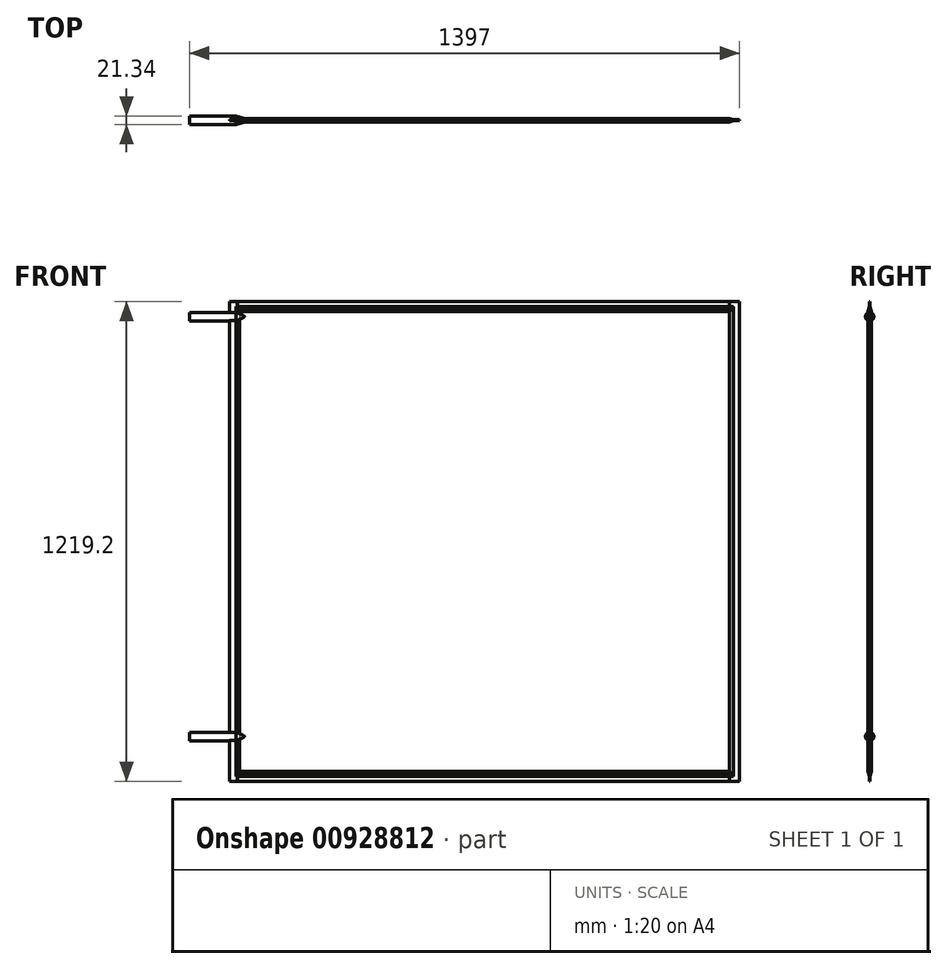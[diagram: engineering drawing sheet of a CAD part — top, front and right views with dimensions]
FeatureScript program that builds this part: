
annotation { "Feature Type Name" : "Feature", "Feature Type Description" : "" }
export const myFeature = defineFeature(function(context is Context, id is Id, definition is map)
    precondition{}
    {
        {
            var Q0;
            Q0=qCreatedBy(makeId("Front.planeOp"),FACE);
            var sketch = newSketch(context, id + "F0", { "sketchPlane" : qUnion([Q0])});
            skLineSegment(sketch, "E0", {"start": v(-991.5, -804.5) * mm, "end": v(-775.6, -1267.5) * mm});
            skLineSegment(sketch, "E1", {"start": v(-991.5, -804.5) * mm, "end": v(-991.5, -829.18) * mm});
            skLineSegment(sketch, "E2", {"start": v(-775.6, -1267.5) * mm, "end": v(-380.3, -1083.18) * mm});
            skLineSegment(sketch, "E3", {"start": v(-380.3, -1083.18) * mm, "end": v(-380.3, -829.18) * mm, "construction": true});
            skLineSegment(sketch, "E4", {"start": v(-991.5, -829.18) * mm, "end": v(-380.3, -829.18) * mm, "construction": true});
            skLineSegment(sketch, "E5", {"start": v(76.1, -804.5) * mm, "end": v(76.1, -359.45) * mm, "construction": true});
            skLineSegment(sketch, "E6", {"start": v(-685.9, -829.18) * mm, "end": v(-685.9, -1225.68) * mm, "construction": true});
            skLineSegment(sketch, "E7.MirrorCS", {"start": v(838.1, -829.18) * mm, "end": v(838.1, -1225.68) * mm, "construction": true});
            skLineSegment(sketch, "E8.MirrorCS", {"start": v(1143.7, -804.5) * mm, "end": v(927.8, -1267.5) * mm, "construction": true});
            skLineSegment(sketch, "E9.MirrorCS", {"start": v(1143.7, -804.5) * mm, "end": v(1143.7, -829.18) * mm, "construction": true});
            skLineSegment(sketch, "E10.MirrorCS", {"start": v(927.8, -1267.5) * mm, "end": v(532.5, -1083.18) * mm, "construction": true});
            skLineSegment(sketch, "E11.MirrorCS", {"start": v(532.5, -1083.18) * mm, "end": v(532.5, -829.18) * mm, "construction": true});
            skLineSegment(sketch, "E12.MirrorCS", {"start": v(1143.7, -829.18) * mm, "end": v(532.5, -829.18) * mm, "construction": true});
            skLineSegment(sketch, "E13", {"start": v(-380.3, -1083.18) * mm, "end": v(76.1, -870.35) * mm});
            skLineSegment(sketch, "E14", {"start": v(76.1, -870.35) * mm, "end": v(532.5, -1083.18) * mm, "construction": true});
            skLineSegment(sketch, "E15", {"start": v(-991.5, -829.18) * mm, "end": v(-991.5, -359.45) * mm});
            skLineSegment(sketch, "E16", {"start": v(-991.5, -359.45) * mm, "end": v(-991.5, -3451.9) * mm, "construction": true});
            skLineSegment(sketch, "E17", {"start": v(-991.5, 1120.1) * mm, "end": v(1143.7, 1120.1) * mm, "construction": true});
            skLineSegment(sketch, "E18", {"start": v(-90.65, 1120.1) * mm, "end": v(-90.65, 1251.48) * mm, "construction": true});
            skLineSegment(sketch, "E19", {"start": v(-90.65, 1251.48) * mm, "end": v(242.85, 1251.48) * mm, "construction": true});
            skLineSegment(sketch, "E20", {"start": v(242.85, 1251.48) * mm, "end": v(242.85, 1120.1) * mm, "construction": true});
            skLineSegment(sketch, "E21", {"start": v(242.85, 1120.1) * mm, "end": v(-90.65, 1120.1) * mm});
            skPoint(sketch, "E22", {"position": v(76.1, 1120.1) * mm});
            skLineSegment(sketch, "E23", {"start": v(-101.7, 1120.1) * mm, "end": v(-101.7, 1251.48) * mm, "construction": true});
            skLineSegment(sketch, "E24", {"start": v(-101.7, 1251.48) * mm, "end": v(253.9, 1251.48) * mm, "construction": true});
            skLineSegment(sketch, "E25", {"start": v(253.9, 1251.48) * mm, "end": v(253.9, 1120.1) * mm, "construction": true});
            skLineSegment(sketch, "E26", {"start": v(253.9, 1120.1) * mm, "end": v(-101.7, 1120.1) * mm, "construction": true});
            skLineSegment(sketch, "E27", {"start": v(-991.5, -359.45) * mm, "end": v(-991.5, 700.03) * mm});
            skLineSegment(sketch, "E28", {"start": v(1143.7, 700.03) * mm, "end": v(1143.7, -829.18) * mm, "construction": true});
            skLineSegment(sketch, "E29", {"start": v(-991.5, 700.03) * mm, "end": v(-991.5, 1120.1) * mm});
            skLineSegment(sketch, "E30", {"start": v(1143.7, 700.03) * mm, "end": v(1143.7, 1120.1) * mm, "construction": true});
            skLineSegment(sketch, "E31", {"start": v(-90.65, 1120.1) * mm, "end": v(-991.5, 700.03) * mm, "construction": true});
            skLineSegment(sketch, "E32", {"start": v(253.9, 1120.1) * mm, "end": v(1143.7, 700.03) * mm, "construction": true});
            skLineSegment(sketch, "E33", {"start": v(-991.5, 1120.1) * mm, "end": v(76.1, 1120.1) * mm});
            skLineSegment(sketch, "E34", {"start": v(76.1, -870.35) * mm, "end": v(76.1, 1120.1) * mm});
            skSolve(sketch);
        }
        {
            var Q0;
            Q0=qCreatedBy(makeId("Front.planeOp"),FACE);
            var sketch = newSketch(context, id + "F1", { "sketchPlane" : qUnion([Q0])});
            skLineSegment(sketch, "E35.0", {"start": v(1422.3, 609.6) * mm, "end": v(1422.3, -609.6) * mm});
            skLineSegment(sketch, "E36", {"start": v(1422.3, -609.6) * mm, "end": v(126.9, -609.6) * mm});
            skLineSegment(sketch, "E37", {"start": v(1422.3, 609.6) * mm, "end": v(126.9, 609.6) * mm});
            skLineSegment(sketch, "E38", {"start": v(126.9, 609.6) * mm, "end": v(126.9, -609.6) * mm});
            skSolve(sketch);
        }
        {
            var Q0;
            Q0=qSketchRegion(id+"F1",true);
            extrude(context, id + "F2", {"entities" : qUnion([Q0]), "endBound" : BoundingType.SYMMETRIC, "depth" : 9.52 * mm, "offsetDistance" : 25.4 * mm});
        }
        {
            var Q0;
            Q0=qCreatedBy(makeId("Top.planeOp"),FACE);
            cPlane(context, id + "F3", {"entities" : qUnion([Q0]), "cplaneType" : CPlaneType.OFFSET, "offset" : 38.1 * mm, "width" : 152.4 * mm, "height" : 152.4 * mm});
        }
        {
            var Q0;
            Q0=qCreatedBy(makeId("Right.planeOp"),FACE);
            var sketch = newSketch(context, id + "F4", { "sketchPlane" : qUnion([Q0])});
            skLineSegment(sketch, "E39", {"start": v(1.21, 609.6) * mm, "end": v(1.21, 593.72) * mm});
            skLineSegment(sketch, "E40", {"start": v(1.21, 584.2) * mm, "end": v(4.76, 584.2) * mm, "construction": true});
            skLineSegment(sketch, "E41", {"start": v(8.31, 584.2) * mm, "end": v(8.31, 615.95) * mm});
            skLineSegment(sketch, "E42", {"start": v(-4.76, 0) * mm, "end": v(4.76, 0) * mm, "construction": true});
            skLineSegment(sketch, "E43", {"start": v(1.21, 596.9) * mm, "end": v(4.76, 584.2) * mm});
            skLineSegment(sketch, "E44", {"start": v(1.21, 593.72) * mm, "end": v(1.21, 584.2) * mm, "construction": true});
            skLineSegment(sketch, "E45", {"start": v(4.76, 584.2) * mm, "end": v(8.31, 584.2) * mm});
            skLineSegment(sketch, "E46", {"start": v(1.21, 609.6) * mm, "end": v(0, 609.6) * mm});
            skLineSegment(sketch, "E47", {"start": v(0, 609.6) * mm, "end": v(0, 615.95) * mm, "construction": true});
            skLineSegment(sketch, "E48", {"start": v(0, 615.95) * mm, "end": v(8.31, 615.95) * mm});
            skLineSegment(sketch, "E49.MirrorCS", {"start": v(-1.21, 609.6) * mm, "end": v(-1.21, 593.72) * mm});
            skLineSegment(sketch, "E50.MirrorCS", {"start": v(-1.21, 596.9) * mm, "end": v(-4.76, 584.2) * mm});
            skLineSegment(sketch, "E51.MirrorCS", {"start": v(-1.21, 609.6) * mm, "end": v(0, 609.6) * mm});
            skLineSegment(sketch, "E52.MirrorCS", {"start": v(0, 615.95) * mm, "end": v(-8.31, 615.95) * mm});
            skLineSegment(sketch, "E53.MirrorCS", {"start": v(-4.76, 584.2) * mm, "end": v(-8.31, 584.2) * mm});
            skLineSegment(sketch, "E54.MirrorCS", {"start": v(-8.31, 584.2) * mm, "end": v(-8.31, 615.95) * mm});
            skLineSegment(sketch, "E55.MirrorCS", {"start": v(-1.21, 593.72) * mm, "end": v(-1.21, 584.2) * mm, "construction": true});
            skLineSegment(sketch, "E56.MirrorCS", {"start": v(-1.21, 584.2) * mm, "end": v(-4.76, 584.2) * mm, "construction": true});
            skLineSegment(sketch, "E57.MirrorCS", {"start": v(1.21, -609.6) * mm, "end": v(0, -609.6) * mm});
            skLineSegment(sketch, "E58.MirrorCS", {"start": v(-1.21, -609.6) * mm, "end": v(0, -609.6) * mm});
            skLineSegment(sketch, "E59.MirrorCS", {"start": v(-8.31, -584.2) * mm, "end": v(-8.31, -615.95) * mm});
            skLineSegment(sketch, "E60.MirrorCS", {"start": v(0, -615.95) * mm, "end": v(8.31, -615.95) * mm});
            skLineSegment(sketch, "E61.MirrorCS", {"start": v(4.76, -584.2) * mm, "end": v(8.31, -584.2) * mm});
            skLineSegment(sketch, "E62.MirrorCS", {"start": v(1.21, -596.9) * mm, "end": v(4.76, -584.2) * mm});
            skLineSegment(sketch, "E63.MirrorCS", {"start": v(1.21, -609.6) * mm, "end": v(1.21, -593.72) * mm});
            skLineSegment(sketch, "E64.MirrorCS", {"start": v(1.21, -584.2) * mm, "end": v(4.76, -584.2) * mm, "construction": true});
            skLineSegment(sketch, "E65.MirrorCS", {"start": v(-1.21, -596.9) * mm, "end": v(-4.76, -584.2) * mm});
            skLineSegment(sketch, "E66.MirrorCS", {"start": v(8.31, -584.2) * mm, "end": v(8.31, -615.95) * mm});
            skLineSegment(sketch, "E67.MirrorCS", {"start": v(-4.76, -584.2) * mm, "end": v(-8.31, -584.2) * mm});
            skLineSegment(sketch, "E68.MirrorCS", {"start": v(1.21, -593.72) * mm, "end": v(1.21, -584.2) * mm, "construction": true});
            skLineSegment(sketch, "E69.MirrorCS", {"start": v(-1.21, -593.72) * mm, "end": v(-1.21, -584.2) * mm, "construction": true});
            skLineSegment(sketch, "E70.MirrorCS", {"start": v(-1.21, -609.6) * mm, "end": v(-1.21, -593.72) * mm});
            skLineSegment(sketch, "E71.MirrorCS", {"start": v(0, -615.95) * mm, "end": v(-8.31, -615.95) * mm});
            skLineSegment(sketch, "E72.MirrorCS", {"start": v(-1.21, -584.2) * mm, "end": v(-4.76, -584.2) * mm, "construction": true});
            skLineSegment(sketch, "E73.MirrorCS", {"start": v(0, -609.6) * mm, "end": v(0, -615.95) * mm, "construction": true});
            skSolve(sketch);
        }
        {
            var Q0;
            Q0=qSketchRegion(id+"F4",true);
            extrude(context, id + "F5", {"entities" : qUnion([Q0]), "operationType" : NewBodyOperationType.REMOVE, "endBound" : BoundingType.THROUGH_ALL, "depth" : 25.4 * mm, "offsetDistance" : 25.4 * mm});
        }
        {
            var Q0;
            Q0=qCreatedBy(makeId("Top.planeOp"),FACE);
            var sketch = newSketch(context, id + "F6", { "sketchPlane" : qUnion([Q0])});
            skLineSegment(sketch, "E74", {"start": v(126.9, 1.21) * mm, "end": v(142.77, 1.21) * mm});
            skLineSegment(sketch, "E75", {"start": v(152.3, 1.21) * mm, "end": v(152.3, 4.76) * mm, "construction": true});
            skLineSegment(sketch, "E76", {"start": v(152.3, 8.31) * mm, "end": v(120.55, 8.31) * mm});
            skLineSegment(sketch, "E77", {"start": v(774.6, 4.76) * mm, "end": v(774.6, -4.76) * mm, "construction": true});
            skLineSegment(sketch, "E78", {"start": v(142.77, 1.21) * mm, "end": v(152.3, 4.76) * mm});
            skLineSegment(sketch, "E79", {"start": v(142.77, 1.21) * mm, "end": v(152.3, 1.21) * mm, "construction": true});
            skLineSegment(sketch, "E80", {"start": v(152.3, 4.76) * mm, "end": v(152.3, 8.31) * mm});
            skLineSegment(sketch, "E81", {"start": v(126.9, 1.21) * mm, "end": v(126.9, 0) * mm});
            skLineSegment(sketch, "E82", {"start": v(126.9, 0) * mm, "end": v(120.55, 0) * mm, "construction": true});
            skLineSegment(sketch, "E83", {"start": v(120.55, 0) * mm, "end": v(120.55, 8.31) * mm});
            skLineSegment(sketch, "E84.MirrorCS", {"start": v(126.9, -1.21) * mm, "end": v(142.77, -1.21) * mm});
            skLineSegment(sketch, "E85.MirrorCS", {"start": v(152.3, -4.76) * mm, "end": v(142.77, -1.21) * mm});
            skLineSegment(sketch, "E86.MirrorCS", {"start": v(126.9, -1.21) * mm, "end": v(126.9, 0) * mm});
            skLineSegment(sketch, "E87.MirrorCS", {"start": v(120.55, 0) * mm, "end": v(120.55, -8.31) * mm});
            skLineSegment(sketch, "E88.MirrorCS", {"start": v(152.3, -4.76) * mm, "end": v(152.3, -8.31) * mm});
            skLineSegment(sketch, "E89.MirrorCS", {"start": v(152.3, -8.31) * mm, "end": v(120.55, -8.31) * mm});
            skLineSegment(sketch, "E90.MirrorCS", {"start": v(142.77, -1.21) * mm, "end": v(152.3, -1.21) * mm, "construction": true});
            skLineSegment(sketch, "E91.MirrorCS", {"start": v(152.3, -1.21) * mm, "end": v(152.3, -4.76) * mm, "construction": true});
            skLineSegment(sketch, "E92.MirrorCS", {"start": v(1422.3, 1.21) * mm, "end": v(1422.3, 0) * mm});
            skLineSegment(sketch, "E93.MirrorCS", {"start": v(1422.3, -1.21) * mm, "end": v(1422.3, 0) * mm});
            skLineSegment(sketch, "E94.MirrorCS", {"start": v(1396.9, 1.21) * mm, "end": v(1396.9, 4.76) * mm, "construction": true});
            skLineSegment(sketch, "E95.MirrorCS", {"start": v(1396.9, -4.76) * mm, "end": v(1396.9, -8.31) * mm});
            skLineSegment(sketch, "E96.MirrorCS", {"start": v(1396.9, -8.31) * mm, "end": v(1428.65, -8.31) * mm});
            skLineSegment(sketch, "E97.MirrorCS", {"start": v(1406.42, 1.21) * mm, "end": v(1396.9, 4.76) * mm});
            skLineSegment(sketch, "E98.MirrorCS", {"start": v(1406.42, 1.21) * mm, "end": v(1396.9, 1.21) * mm, "construction": true});
            skLineSegment(sketch, "E99.MirrorCS", {"start": v(1396.9, -1.21) * mm, "end": v(1396.9, -4.76) * mm, "construction": true});
            skLineSegment(sketch, "E100.MirrorCS", {"start": v(1428.65, 0) * mm, "end": v(1428.65, 8.31) * mm});
            skLineSegment(sketch, "E101.MirrorCS", {"start": v(1428.65, 0) * mm, "end": v(1428.65, -8.31) * mm});
            skLineSegment(sketch, "E102.MirrorCS", {"start": v(1422.3, 1.21) * mm, "end": v(1406.42, 1.21) * mm});
            skLineSegment(sketch, "E103.MirrorCS", {"start": v(1396.9, 8.31) * mm, "end": v(1428.65, 8.31) * mm});
            skLineSegment(sketch, "E104.MirrorCS", {"start": v(1396.9, 4.76) * mm, "end": v(1396.9, 8.31) * mm});
            skLineSegment(sketch, "E105.MirrorCS", {"start": v(1422.3, 0) * mm, "end": v(1428.65, 0) * mm, "construction": true});
            skLineSegment(sketch, "E106.MirrorCS", {"start": v(1422.3, -1.21) * mm, "end": v(1406.42, -1.21) * mm});
            skLineSegment(sketch, "E107.MirrorCS", {"start": v(1396.9, -4.76) * mm, "end": v(1406.42, -1.21) * mm});
            skLineSegment(sketch, "E108.MirrorCS", {"start": v(1406.42, -1.21) * mm, "end": v(1396.9, -1.21) * mm, "construction": true});
            skSolve(sketch);
        }
        {
            var Q0;
            Q0=qSketchRegion(id+"F6",true);
            extrude(context, id + "F7", {"entities" : qUnion([Q0]), "operationType" : NewBodyOperationType.REMOVE, "endBound" : BoundingType.THROUGH_ALL, "oppositeDirection" : true, "depth" : 25.4 * mm, "offsetDistance" : 25.4 * mm, "hasSecondDirection" : true, "secondDirectionBound" : SecondDirectionBoundingType.THROUGH_ALL, "secondDirectionOppositeDirection" : false, "secondDirectionDepth" : 25.4 * mm});
        }
        {
            var Q0;
            Q0=qCreatedBy(makeId("Front.planeOp"),FACE);
            var sketch = newSketch(context, id + "F8", { "sketchPlane" : qUnion([Q0])});
            skLineSegment(sketch, "E109", {"start": v(25.3, 571.5) * mm, "end": v(25.3, 582.17) * mm});
            skLineSegment(sketch, "E110", {"start": v(25.3, 582.17) * mm, "end": v(142.77, 582.17) * mm});
            skLineSegment(sketch, "E111", {"start": v(142.77, 582.17) * mm, "end": v(164.81, 576.26) * mm});
            skLineSegment(sketch, "E112", {"start": v(164.81, 576.26) * mm, "end": v(164.81, 571.5) * mm});
            skLineSegment(sketch, "E113", {"start": v(164.81, 571.5) * mm, "end": v(25.3, 571.5) * mm});
            skSolve(sketch);
        }
        {
            var Q0;
            Q0=qSketchRegion(id+"F8",true);
            var Q1;
            Q1=qConstructionFilter(qBodyType(qCreatedBy(id+"F8",EDGE),BodyType.WIRE),ConstructionObject.NO);
            var Q2;
            Q2=sQuery(id+"F8.wireOp",EDGE,"E113");
            revolve(context, id + "F9", {"entities" : qUnion([Q0]), "surfaceEntities" : qUnion([Q1]), "axis" : qUnion([Q2]), "revolveType" : RevolveType.FULL});
        }
        {
            var Q0;
            Q0=makeQuery(id+"F9.opRevolve","SWEPT_BODY",BODY,{"disambiguationData":[OSD([sQuery(id+"F8.wireOp",EDGE,"E109"),sQuery(id+"F8.wireOp",EDGE,"E110"),sQuery(id+"F8.wireOp",EDGE,"E111"),sQuery(id+"F8.wireOp",EDGE,"E112"),sQuery(id+"F8.wireOp",EDGE,"E113")])]});
            var Q1;
            Q1=qCreatedBy(id+"F3.planeOp",FACE);
            mirror(context, id + "F10", {"entities" : qUnion([Q0]), "mirrorPlane" : qUnion([Q1])});
        }
        {
            var Q0;
            Q0=makeQuery(id+"F2.opExtrude","SWEPT_BODY",BODY,{"disambiguationData":[OSD([sQuery(id+"F1.wireOp",EDGE,"E35.0"),sQuery(id+"F1.wireOp",EDGE,"E36"),sQuery(id+"F1.wireOp",EDGE,"E37"),sQuery(id+"F1.wireOp",EDGE,"E38")])]});
            var Q1;
            Q1=makeQuery(id+"F9.opRevolve","SWEPT_BODY",BODY,{"disambiguationData":[OSD([sQuery(id+"F8.wireOp",EDGE,"E109"),sQuery(id+"F8.wireOp",EDGE,"E110"),sQuery(id+"F8.wireOp",EDGE,"E111"),sQuery(id+"F8.wireOp",EDGE,"E112"),sQuery(id+"F8.wireOp",EDGE,"E113")])]});
            var Q2;
            Q2=makeQuery(id+"F10.opPattern","COPY",BODY,{"derivedFrom":makeQuery(id+"F9.opRevolve","SWEPT_BODY",BODY,{"disambiguationData":[OSD([sQuery(id+"F8.wireOp",EDGE,"E109"),sQuery(id+"F8.wireOp",EDGE,"E110"),sQuery(id+"F8.wireOp",EDGE,"E111"),sQuery(id+"F8.wireOp",EDGE,"E112"),sQuery(id+"F8.wireOp",EDGE,"E113")])]}),"instanceName":"1"});
            booleanBodies(context, id + "F11", {"operationType" : BooleanOperationType.UNION, "tools" : qUnion([Q0, Q1, Q2])});
        }
        {
            var Q0;
            Q0=qCreatedBy(makeId("Top.planeOp"),FACE);
            var sketch = newSketch(context, id + "F12", { "sketchPlane" : qUnion([Q0])});
            skLineSegment(sketch, "E114.0", {"start": v(1396.62, -3.24) * mm, "end": v(152.57, -3.24) * mm});
            skLineSegment(sketch, "E114.1", {"start": v(152.57, -3.24) * mm, "end": v(143.88, 0) * mm});
            skLineSegment(sketch, "E114.2", {"start": v(143.88, 0) * mm, "end": v(152.57, 3.24) * mm});
            skFitSpline(sketch, "E114.3", {"points": [v(152.57, 3.24) * mm, v(156.65, 3.24) * mm, v(160.73, 3.24) * mm, v(164.81, 3.24) * mm]});
            skLineSegment(sketch, "E114.4", {"start": v(1396.62, 3.24) * mm, "end": v(152.57, 3.24) * mm});
            skLineSegment(sketch, "E114.5", {"start": v(1396.62, -3.24) * mm, "end": v(1396.62, -3.24) * mm});
            skLineSegment(sketch, "E114.6", {"start": v(1396.62, 3.24) * mm, "end": v(1396.62, 3.24) * mm});
            skLineSegment(sketch, "E115.left", {"start": v(1396.62, -3.24) * mm, "end": v(1396.62, 3.24) * mm});
            skLineSegment(sketch, "E115.right", {"start": v(1396.62, -3.24) * mm, "end": v(1396.62, 3.24) * mm});
            skSolve(sketch);
        }
        {
            var Q0;
            Q0=qSketchRegion(id+"F12",true);
            var Q1;
            Q1=makeQuery(id+"F2.opExtrude","SWEPT_BODY",BODY,{"disambiguationData":[OSD([sQuery(id+"F1.wireOp",EDGE,"E35.0"),sQuery(id+"F1.wireOp",EDGE,"E36"),sQuery(id+"F1.wireOp",EDGE,"E37"),sQuery(id+"F1.wireOp",EDGE,"E38")])]});
            var Q2;
            Q2=makeQuery(id+"F2.opExtrude","SWEPT_BODY",BODY,{"disambiguationData":[OSD([sQuery(id+"F1.wireOp",EDGE,"E35.0"),sQuery(id+"F1.wireOp",EDGE,"E36"),sQuery(id+"F1.wireOp",EDGE,"E37"),sQuery(id+"F1.wireOp",EDGE,"E38")])]});
            extrude(context, id + "F13", {"entities" : qUnion([Q0]), "endBound" : BoundingType.UP_TO_BODY, "depth" : 25.4 * mm, "endBoundEntityBody" : qUnion([Q1]), "offsetDistance" : 25.4 * mm, "hasSecondDirection" : true, "secondDirectionBound" : SecondDirectionBoundingType.UP_TO_BODY, "secondDirectionOppositeDirection" : true, "secondDirectionDepth" : 25.4 * mm, "secondDirectionBoundEntityBody" : qUnion([Q2])});
        }
    });
